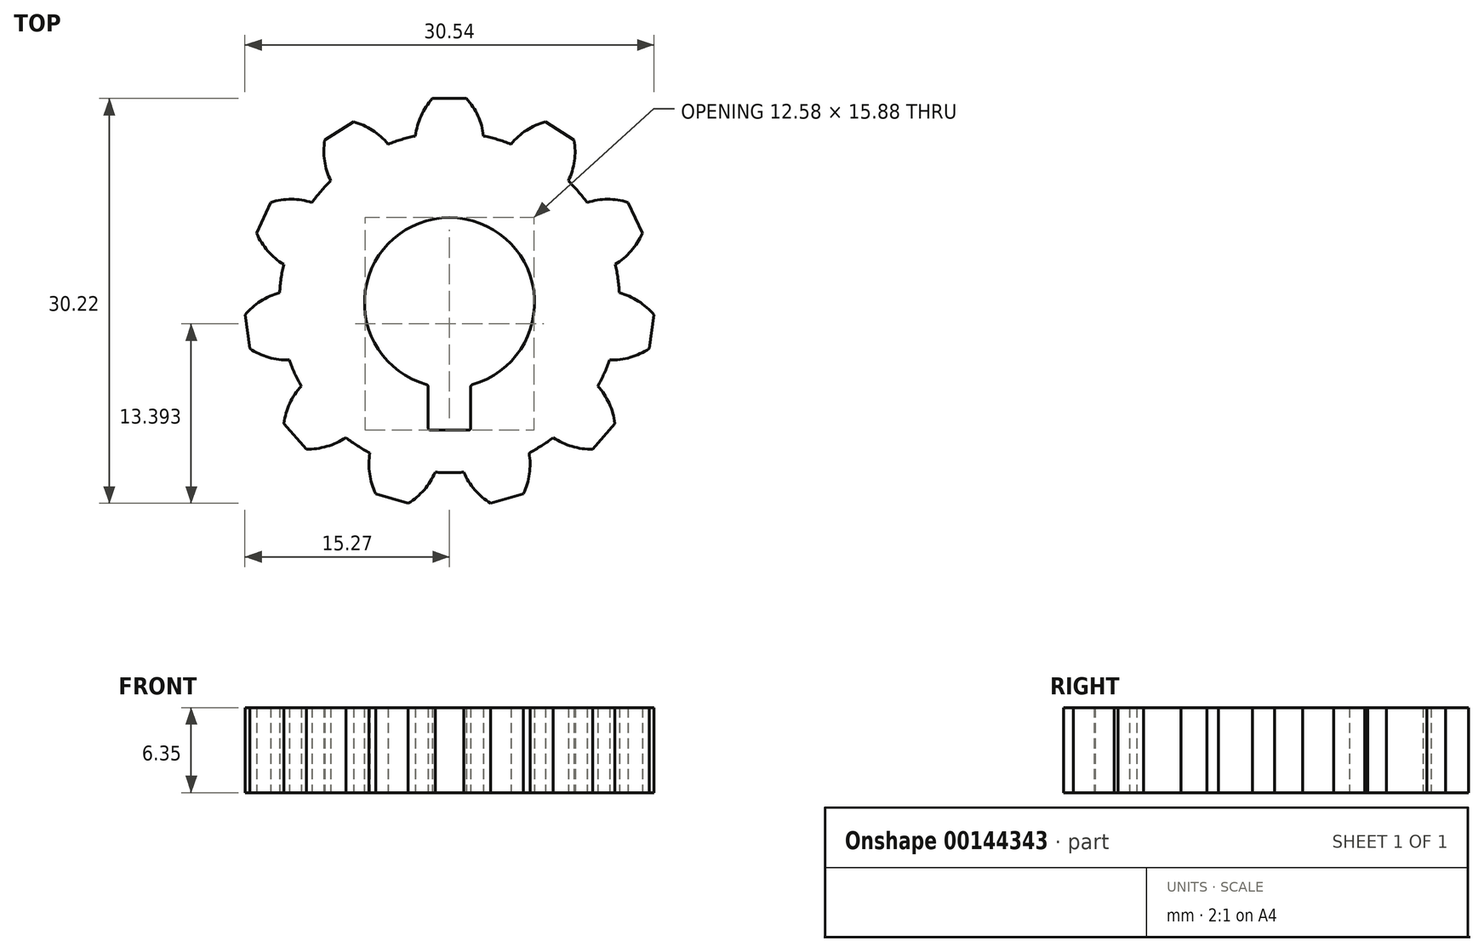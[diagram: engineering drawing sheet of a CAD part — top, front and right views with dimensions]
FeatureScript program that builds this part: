
annotation { "Feature Type Name" : "Feature", "Feature Type Description" : "" }
export const myFeature = defineFeature(function(context is Context, id is Id, definition is map)
    precondition{}
    {
        {
            var Q0;
            Q0=qCreatedBy(makeId("Top.planeOp"),FACE);
            var sketch = newSketch(context, id + "F0", { "sketchPlane" : qUnion([Q0])});
            skArc(sketch, "E0", {"start": v(-1.07, -12.65) * mm, "mid": v(0, -12.7) * mm, "end": v(1.07, -12.65) * mm, "construction": true});
            skArc(sketch, "E1", {"start": v(-1.27, 15.24) * mm, "mid": v(-2.12, 13.94) * mm, "end": v(-2.54, 12.44) * mm});
            skLineSegment(sketch, "E2", {"start": v(-1.27, 15.24) * mm, "end": v(1.27, 15.24) * mm});
            skArc(sketch, "E3", {"start": v(2.54, 12.44) * mm, "mid": v(2.12, 13.94) * mm, "end": v(1.27, 15.24) * mm});
            skLineSegment(sketch, "E4", {"start": v(0, 15.24) * mm, "end": v(0, 0) * mm, "construction": true});
            skLineSegment(sketch, "E5", {"start": v(-2.54, 12.44) * mm, "end": v(2.54, 12.44) * mm, "construction": true});
            skLineSegment(sketch, "E6.1.0", {"start": v(-9.3, 12.13) * mm, "end": v(-7.17, 13.5) * mm});
            skArc(sketch, "E6.1.1", {"start": v(-9.3, 12.13) * mm, "mid": v(-9.32, 10.58) * mm, "end": v(-8.86, 9.1) * mm});
            skArc(sketch, "E6.1.2", {"start": v(-4.6, 11.84) * mm, "mid": v(-5.75, 12.87) * mm, "end": v(-7.17, 13.5) * mm});
            skLineSegment(sketch, "E6.2.0", {"start": v(-14.4, 5.18) * mm, "end": v(-13.34, 7.49) * mm});
            skArc(sketch, "E6.2.1", {"start": v(-14.4, 5.18) * mm, "mid": v(-13.56, 3.86) * mm, "end": v(-12.37, 2.86) * mm});
            skArc(sketch, "E6.2.2", {"start": v(-10.26, 7.48) * mm, "mid": v(-11.8, 7.72) * mm, "end": v(-13.34, 7.49) * mm});
            skLineSegment(sketch, "E6.3.0", {"start": v(-14.9, -3.43) * mm, "end": v(-15.27, -0.91) * mm});
            skArc(sketch, "E6.3.1", {"start": v(-14.9, -3.43) * mm, "mid": v(-13.5, -4.08) * mm, "end": v(-11.96, -4.29) * mm});
            skArc(sketch, "E6.3.2", {"start": v(-12.68, 0.74) * mm, "mid": v(-14.1, 0.12) * mm, "end": v(-15.27, -0.91) * mm});
            skLineSegment(sketch, "E6.4.0", {"start": v(-10.69, -10.94) * mm, "end": v(-12.35, -9.02) * mm});
            skArc(sketch, "E6.4.1", {"start": v(-10.69, -10.94) * mm, "mid": v(-9.15, -10.73) * mm, "end": v(-7.74, -10.07) * mm});
            skArc(sketch, "E6.4.2", {"start": v(-11.07, -6.23) * mm, "mid": v(-11.92, -7.53) * mm, "end": v(-12.35, -9.02) * mm});
            skLineSegment(sketch, "E6.5.0", {"start": v(-3.08, -14.98) * mm, "end": v(-5.51, -14.26) * mm});
            skArc(sketch, "E6.5.1", {"start": v(-3.08, -14.98) * mm, "mid": v(-1.9, -13.97) * mm, "end": v(-1.07, -12.65) * mm});
            skArc(sketch, "E6.5.2", {"start": v(-5.94, -11.22) * mm, "mid": v(-5.96, -12.78) * mm, "end": v(-5.51, -14.26) * mm});
            skArc(sketch, "E7", {"start": v(-8.86, 9.1) * mm, "mid": v(-9.6, 8.32) * mm, "end": v(-10.26, 7.48) * mm});
            skArc(sketch, "E8.trimOffspring", {"start": v(-2.54, 12.44) * mm, "mid": v(-3.58, 12.19) * mm, "end": v(-4.6, 11.84) * mm});
            skArc(sketch, "E9.trimOffspring", {"start": v(4.6, 11.84) * mm, "mid": v(3.58, 12.19) * mm, "end": v(2.54, 12.44) * mm});
            skArc(sketch, "E10.trimOffspring", {"start": v(-7.74, -10.07) * mm, "mid": v(-6.87, -10.68) * mm, "end": v(-5.94, -11.22) * mm});
            skArc(sketch, "E11.trimOffspring", {"start": v(-11.96, -4.29) * mm, "mid": v(-11.55, -5.28) * mm, "end": v(-11.07, -6.23) * mm});
            skArc(sketch, "E12.trimOffspring", {"start": v(-12.37, 2.86) * mm, "mid": v(-12.57, 1.8) * mm, "end": v(-12.68, 0.74) * mm});
            skLineSegment(sketch, "E13.1.6.0", {"start": v(5.51, -14.26) * mm, "end": v(3.08, -14.98) * mm});
            skArc(sketch, "E13.3.6.0", {"start": v(5.51, -14.26) * mm, "mid": v(5.96, -12.78) * mm, "end": v(5.94, -11.22) * mm});
            skArc(sketch, "E13.7.6.0", {"start": v(1.07, -12.65) * mm, "mid": v(1.9, -13.97) * mm, "end": v(3.08, -14.98) * mm});
            skLineSegment(sketch, "E13.1.7.0", {"start": v(12.35, -9.02) * mm, "end": v(10.69, -10.94) * mm});
            skArc(sketch, "E13.3.7.0", {"start": v(12.35, -9.02) * mm, "mid": v(11.92, -7.53) * mm, "end": v(11.07, -6.23) * mm});
            skArc(sketch, "E13.7.7.0", {"start": v(7.74, -10.07) * mm, "mid": v(9.15, -10.73) * mm, "end": v(10.69, -10.94) * mm});
            skLineSegment(sketch, "E13.1.8.0", {"start": v(15.27, -0.91) * mm, "end": v(14.9, -3.43) * mm});
            skArc(sketch, "E13.3.8.0", {"start": v(15.27, -0.91) * mm, "mid": v(14.1, 0.12) * mm, "end": v(12.68, 0.74) * mm});
            skArc(sketch, "E13.7.8.0", {"start": v(11.96, -4.29) * mm, "mid": v(13.5, -4.08) * mm, "end": v(14.9, -3.43) * mm});
            skLineSegment(sketch, "E13.1.9.0", {"start": v(13.34, 7.49) * mm, "end": v(14.4, 5.18) * mm});
            skArc(sketch, "E13.3.9.0", {"start": v(13.34, 7.49) * mm, "mid": v(11.8, 7.72) * mm, "end": v(10.26, 7.48) * mm});
            skArc(sketch, "E13.7.9.0", {"start": v(12.37, 2.86) * mm, "mid": v(13.56, 3.86) * mm, "end": v(14.4, 5.18) * mm});
            skLineSegment(sketch, "E14.1.10.0", {"start": v(7.17, 13.5) * mm, "end": v(9.3, 12.13) * mm});
            skArc(sketch, "E14.3.10.0", {"start": v(7.17, 13.5) * mm, "mid": v(5.75, 12.87) * mm, "end": v(4.6, 11.84) * mm});
            skArc(sketch, "E14.7.10.0", {"start": v(8.86, 9.1) * mm, "mid": v(9.32, 10.58) * mm, "end": v(9.3, 12.13) * mm});
            skArc(sketch, "E15", {"start": v(1.71, -6.11) * mm, "mid": v(0, 6.35) * mm, "end": v(-1.71, -6.11) * mm});
            skLineSegment(sketch, "E16", {"start": v(-1.59, -6.28) * mm, "end": v(-1.59, -9.35) * mm});
            skLineSegment(sketch, "E17", {"start": v(-1.41, -9.53) * mm, "end": v(1.41, -9.53) * mm});
            skLineSegment(sketch, "E18", {"start": v(1.59, -9.35) * mm, "end": v(1.59, -6.28) * mm});
            skLineSegment(sketch, "E19", {"start": v(0, -9.53) * mm, "end": v(0, 0) * mm, "construction": true});
            skPoint(sketch, "E20.visualSharp", {"position": v(-1.59, -6.15) * mm});
            skArc(sketch, "E20.filletArc", {"start": v(-1.59, -6.28) * mm, "mid": v(-1.62, -6.18) * mm, "end": v(-1.71, -6.11) * mm});
            skPoint(sketch, "E21.visualSharp", {"position": v(1.59, -6.15) * mm});
            skArc(sketch, "E21.filletArc", {"start": v(1.71, -6.11) * mm, "mid": v(1.62, -6.18) * mm, "end": v(1.59, -6.28) * mm});
            skPoint(sketch, "E22.visualSharp", {"position": v(-1.59, -9.53) * mm});
            skArc(sketch, "E22.filletArc", {"start": v(-1.59, -9.35) * mm, "mid": v(-1.54, -9.47) * mm, "end": v(-1.41, -9.53) * mm});
            skPoint(sketch, "E23.visualSharp", {"position": v(1.59, -9.53) * mm});
            skArc(sketch, "E23.filletArc", {"start": v(1.41, -9.53) * mm, "mid": v(1.54, -9.47) * mm, "end": v(1.59, -9.35) * mm});
            skArc(sketch, "E24.trimOffspring", {"start": v(-1.07, -12.65) * mm, "mid": v(0, -12.7) * mm, "end": v(1.07, -12.65) * mm});
            skArc(sketch, "E25.trimOffspring", {"start": v(5.94, -11.22) * mm, "mid": v(6.87, -10.68) * mm, "end": v(7.74, -10.07) * mm, "construction": true});
            skArc(sketch, "E26.trimOffspring", {"start": v(5.94, -11.22) * mm, "mid": v(6.87, -10.68) * mm, "end": v(7.74, -10.07) * mm});
            skArc(sketch, "E27.trimOffspring", {"start": v(11.07, -6.23) * mm, "mid": v(11.55, -5.28) * mm, "end": v(11.96, -4.29) * mm, "construction": true});
            skArc(sketch, "E28.trimOffspring", {"start": v(11.07, -6.23) * mm, "mid": v(11.55, -5.28) * mm, "end": v(11.96, -4.29) * mm});
            skArc(sketch, "E29.trimOffspring", {"start": v(12.68, 0.74) * mm, "mid": v(12.57, 1.8) * mm, "end": v(12.37, 2.86) * mm, "construction": true});
            skArc(sketch, "E30.trimOffspring", {"start": v(12.68, 0.74) * mm, "mid": v(12.57, 1.8) * mm, "end": v(12.37, 2.86) * mm});
            skArc(sketch, "E31.trimOffspring", {"start": v(10.26, 7.48) * mm, "mid": v(9.6, 8.32) * mm, "end": v(8.86, 9.1) * mm, "construction": true});
            skArc(sketch, "E32.trimOffspring", {"start": v(10.26, 7.48) * mm, "mid": v(9.6, 8.32) * mm, "end": v(8.86, 9.1) * mm});
            skArc(sketch, "E33.trimOffspring", {"start": v(4.6, 11.84) * mm, "mid": v(3.58, 12.19) * mm, "end": v(2.54, 12.44) * mm, "construction": true});
            skArc(sketch, "E34.trimOffspring", {"start": v(-2.54, 12.44) * mm, "mid": v(-3.58, 12.19) * mm, "end": v(-4.6, 11.84) * mm, "construction": true});
            skArc(sketch, "E35.trimOffspring", {"start": v(-8.86, 9.1) * mm, "mid": v(-9.6, 8.32) * mm, "end": v(-10.26, 7.48) * mm, "construction": true});
            skArc(sketch, "E36.trimOffspring", {"start": v(-12.37, 2.86) * mm, "mid": v(-12.57, 1.8) * mm, "end": v(-12.68, 0.74) * mm, "construction": true});
            skArc(sketch, "E37.trimOffspring", {"start": v(-11.96, -4.29) * mm, "mid": v(-11.55, -5.28) * mm, "end": v(-11.07, -6.23) * mm, "construction": true});
            skArc(sketch, "E38.trimOffspring", {"start": v(-7.74, -10.07) * mm, "mid": v(-6.87, -10.68) * mm, "end": v(-5.94, -11.22) * mm, "construction": true});
            skSolve(sketch);
        }
        {
            var Q0;
            Q0 = qSketchRegion(id + "F0", true);
            extrude(context, id + "F1", {"entities" : qUnion([Q0]), "depth" : 6.35 * mm});
        }
    });
